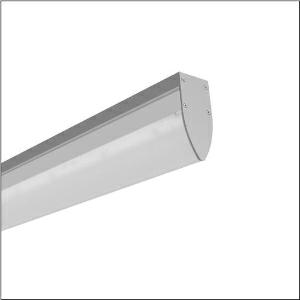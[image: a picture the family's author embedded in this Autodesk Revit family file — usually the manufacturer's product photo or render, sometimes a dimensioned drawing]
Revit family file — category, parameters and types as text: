
# Revit family: mira_21_td_51fr527k444a
name_source: partatom
category: Lighting Fixtures
units: mm (PartAtom-declared; Revit-internal decimal feet)

## family parameters
Cut with Voids When Loaded = No
Host = Face
Light Source = No
Part Type = Normal
Room Calculation Point = No
Round Connector Dimension = Use Diameter
Shared = No

## types (1)
- Mira 21 TD (1 x LED, 4030 lm, 27 W, 4000K)
    Apparent Load = 27 VA
    CIE Flux Codes = 40 68 87 81 100
    Color Rendering = 80
    Color Temperature = 4000K
    Default Elevation = 1800 mm
    Description = Mira 21 TD, clean room luminaire, primary light control with reflector, primary optical cover: cover, of PMMA, frosted, light emission: direct distribution, primary light characteristic: symmetric, installation type: surface-mounted, LED, rated luminous flux: 4.030lm, luminous efficacy: 149lm/W, light colour: 840, colour temperature: 4000K, control gear: ON/OFF, with terminal, 3-pole, max. 2.5mm², mains connection: 230V, AC, 50/60Hz, rated input power: 27W, luminaire housing, of sheet steel, coated, pure white (RAL 9010), length: 1.200mm, width: 55mm, height: 120mm, protection rating (complete): IP43, insulation class (complete): insulation class I (protective earthing), certification: CE, UKCA, permissible operating ambient temperature: -5..+40°C, standard: EN 50419, packaging unit: 1 piece
    Height = 120 mm
    Lamp = 1 x LED
    Lamp Light Flux = 4030 lm
    Lamp Power = 27 W
    Lamp count = 1
    Length = 1200 mm
    Luminous efficacy = 149 lm/W
    Manufacturer = Siteco
    ModVariant = No
    Model = 51FR527K444A
    Mounting Place = Ceiling
    Mounting Type = Surface mounted
    Number of Poles = 1
    OnlyDefault = Yes
    Power Factor = 1
    Product Name = Mira 21 TD
    Product group = clean room luminaire | ceiling mounted
    ProductGroupID = 306
    Protection Class = Protection class I
    Protection Degree = IP 43
    RLX_Detail_Level = 1
    RLX_Emergency_Light_Flux = 0 lm
    RLX_Emergency_Type = 0
    RLX_Emergency_Type_DB = No
    RlxData = <blob elided: 25157 chars, md5=afe1cfd1>
    Socket = socket
    Standby Power = 0 W
    System Light Flux = 4030 lm
    System Power = 27 W
    Type Comments = Product without accessories
    Type Image = l_1007115.jpg
    URL = http://relux.com
    VarID = ---
    Voltage = 0 V
    Weight = 0.00 kg
    Width = 55 mm

## geometry (parser evidence)
native form markers: Blend x4, Sweep x12
no freeform markers — native parametric forms only
